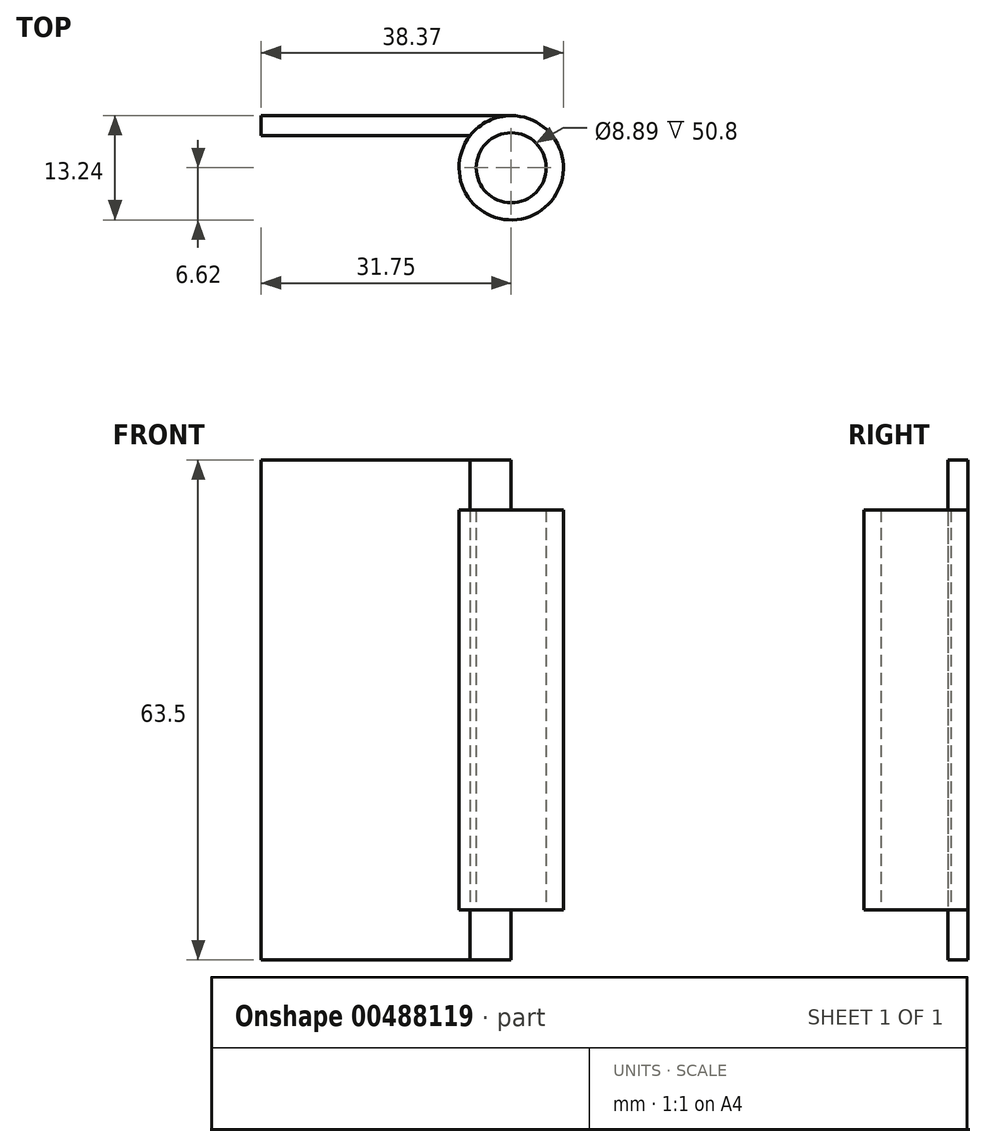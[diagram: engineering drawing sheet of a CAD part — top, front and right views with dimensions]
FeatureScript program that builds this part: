
annotation { "Feature Type Name" : "Feature", "Feature Type Description" : "" }
export const myFeature = defineFeature(function(context is Context, id is Id, definition is map)
    precondition{}
    {
        {
            var Q0;
            Q0=qCreatedBy(makeId("Top.planeOp"),FACE);
            var sketch = newSketch(context, id + "F0", { "sketchPlane" : qUnion([Q0])});
            skCircle(sketch, "E0", {"center": v(0, 0) * mm, "radius": 6.62 * mm});
            skCircle(sketch, "E1", {"center": v(0, 0) * mm, "radius": 4.45 * mm});
            skLineSegment(sketch, "E2", {"start": v(0, 6.62) * mm, "end": v(-31.75, 6.62) * mm});
            skLineSegment(sketch, "E3", {"start": v(-31.75, 6.62) * mm, "end": v(-31.75, 4.08) * mm});
            skLineSegment(sketch, "E4", {"start": v(-31.75, 4.08) * mm, "end": v(-5.21, 4.08) * mm});
            skArc(sketch, "E5", {"start": v(0, 6.62) * mm, "mid": v(-2.9, 5.95) * mm, "end": v(-5.21, 4.08) * mm});
            skSolve(sketch);
        }
        {
            var Q0;
            Q0=makeQuery(id+"F0.imprint","IMPRINT",FACE,{"disambiguationData":[TD([[makeQuery(id+"F0.imprint","IMPRINT",EDGE,{"derivedFrom":sQuery(id+"F0.wireOp",EDGE,"E1")}),-1.0]])]});
            extrude(context, id + "F1", {"entities" : qUnion([Q0]), "endBound" : BoundingType.SYMMETRIC, "depth" : 50.8 * mm, "offsetDistance" : 25.4 * mm});
        }
        {
            var Q0;
            {var subQ0=sQuery(id+"F0.wireOp",EDGE,"E2");Q0=makeQuery(id+"F0.imprint","IMPRINT",FACE,{"disambiguationData":[TD([[makeQuery(id+"F0.imprint","IMPRINT",EDGE,{"derivedFrom":subQ0}),1.0]])]});}
            extrude(context, id + "F2", {"entities" : qUnion([Q0]), "operationType" : NewBodyOperationType.ADD, "endBound" : BoundingType.SYMMETRIC, "depth" : 63.5 * mm, "offsetDistance" : 25.4 * mm});
        }
    });
